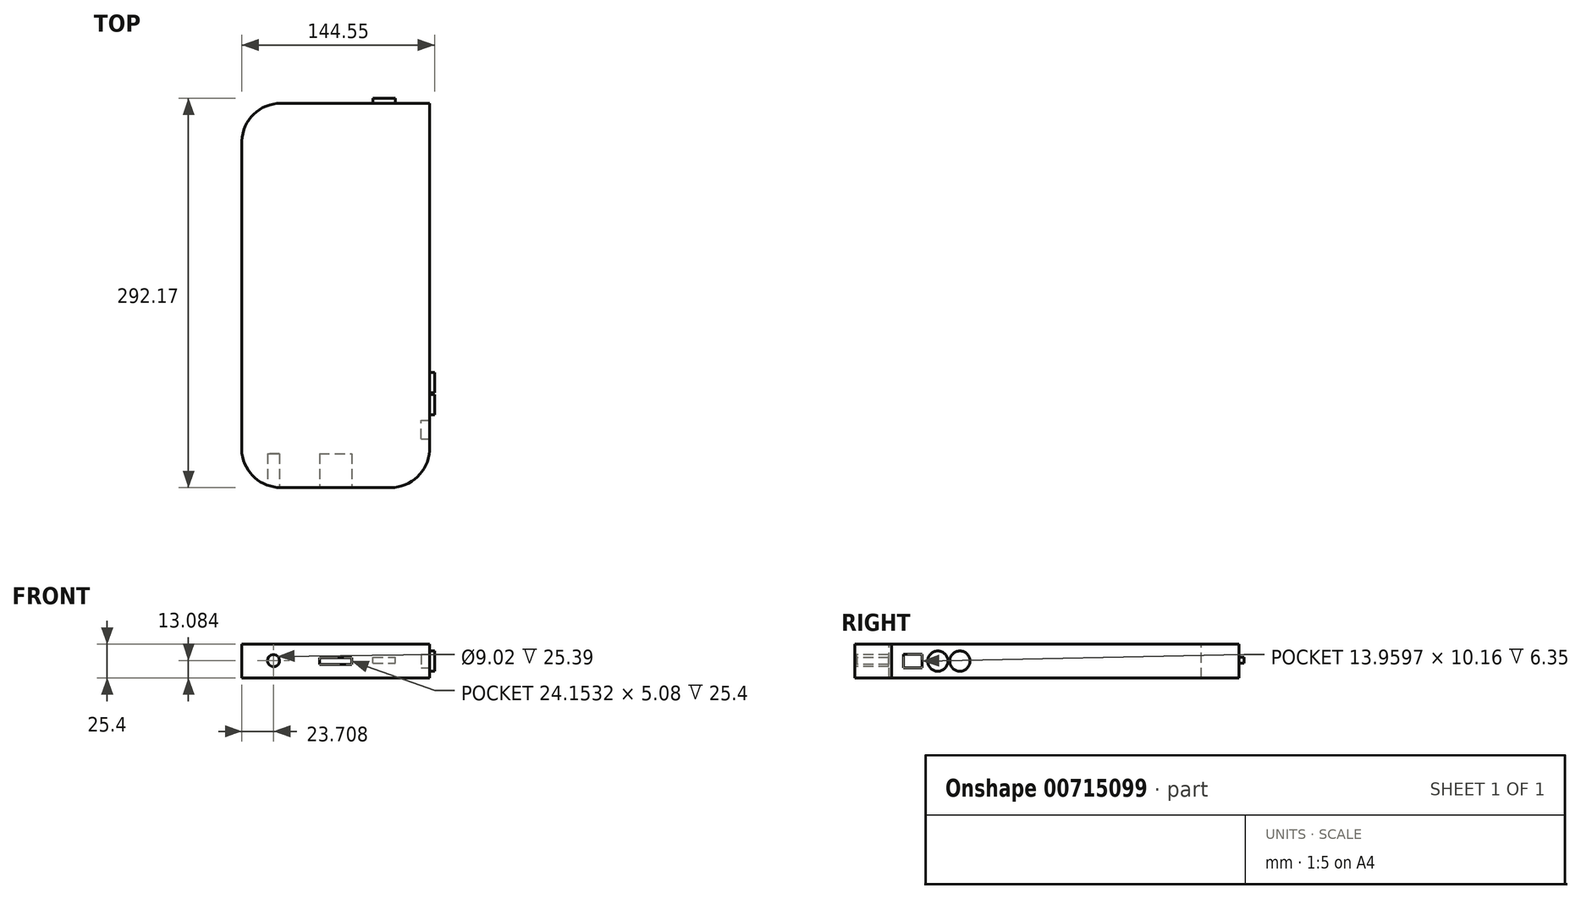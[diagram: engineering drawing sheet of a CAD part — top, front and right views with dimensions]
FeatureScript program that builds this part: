
annotation { "Feature Type Name" : "Feature", "Feature Type Description" : "" }
export const myFeature = defineFeature(function(context is Context, id is Id, definition is map)
    precondition{}
    {
        {
            var Q0;
            Q0=qCreatedBy(makeId("Top.planeOp"),FACE);
            var sketch = newSketch(context, id + "F0", { "sketchPlane" : qUnion([Q0])});
            skLineSegment(sketch, "E0.bottom", {"start": v(-74.1, 116.3) * mm, "end": v(66.65, 116.3) * mm});
            skLineSegment(sketch, "E0.top", {"start": v(-74.1, -172.07) * mm, "end": v(66.65, -172.07) * mm});
            skLineSegment(sketch, "E0.left", {"start": v(-74.1, 116.3) * mm, "end": v(-74.1, -172.07) * mm});
            skLineSegment(sketch, "E0.right", {"start": v(66.65, 116.3) * mm, "end": v(66.65, -172.07) * mm});
            skSolve(sketch);
        }
        {
            var Q0;
            Q0 = qSketchRegion(id + "F0", true);
            extrude(context, id + "F1", {"entities" : qUnion([Q0]), "depth" : 25.4 * mm, "offsetDistance" : 25.4 * mm});
        }
        {
            var Q0;
            Q0=makeQuery(id+"F1.opExtrude","CAP_FACE",FACE,{"disambiguationData":[OSD([sQuery(id+"F0.wireOp",EDGE,"E0.bottom"),sQuery(id+"F0.wireOp",EDGE,"E0.top"),sQuery(id+"F0.wireOp",EDGE,"E0.left"),sQuery(id+"F0.wireOp",EDGE,"E0.right")])],"isStart":false});
            var sketch = newSketch(context, id + "F2", { "sketchPlane" : qUnion([Q0])});
            skArc(sketch, "E1", {"start": v(37.48, -172.07) * mm, "mid": v(57.6, -164.03) * mm, "end": v(66.65, -144.34) * mm});
            skArc(sketch, "E2", {"start": v(-74.1, -139.36) * mm, "mid": v(-66.95, -162.24) * mm, "end": v(-45.1, -172.07) * mm});
            skArc(sketch, "E3", {"start": v(66.65, 85.36) * mm, "mid": v(57.56, 108.56) * mm, "end": v(33.87, 116.3) * mm});
            skArc(sketch, "E4", {"start": v(-44.9, 116.3) * mm, "mid": v(-65.83, 107.45) * mm, "end": v(-74.1, 86.27) * mm});
            skSolve(sketch);
        }
        {
            var Q0;
            {var subQ7=sQuery(id+"F2.wireOp",EDGE,"E1");Q0=makeQuery(id+"F2.imprint","IMPRINT",FACE,{"disambiguationData":[TD([[makeQuery(id+"F2.imprint","IMPRINT",EDGE,{"derivedFrom":subQ7}),1.0]])]});}
            var sketch = newSketch(context, id + "F3", { "sketchPlane" : qUnion([Q0])});
            skLineSegment(sketch, "E5.bottom", {"start": v(-61.4, -116.5) * mm, "end": v(53.95, -116.5) * mm});
            skLineSegment(sketch, "E5.top", {"start": v(-61.4, 71.84) * mm, "end": v(53.95, 71.84) * mm});
            skLineSegment(sketch, "E5.left", {"start": v(-61.4, -116.5) * mm, "end": v(-61.4, 71.84) * mm});
            skLineSegment(sketch, "E5.right", {"start": v(53.95, -116.5) * mm, "end": v(53.95, 71.84) * mm});
            skCircle(sketch, "E6", {"center": v(-9.17, -146.33) * mm, "radius": 13.88 * mm});
            skArc(sketch, "E7", {"start": v(-43.18, -172.58) * mm, "mid": v(-66.38, -163.17) * mm, "end": v(-73.78, -139.25) * mm});
            skArc(sketch, "E8", {"start": v(67.46, -143.84) * mm, "mid": v(57.83, -163.2) * mm, "end": v(37.53, -170.64) * mm});
            skArc(sketch, "E9", {"start": v(34.57, 116.43) * mm, "mid": v(58.51, 108.08) * mm, "end": v(66.9, 84.15) * mm});
            skArc(sketch, "E10", {"start": v(-45.12, 117.02) * mm, "mid": v(-67.2, 107.18) * mm, "end": v(-74.31, 84.07) * mm});
            skSolve(sketch);
        }
        {
            var Q0;
            {var subQ0=sQuery(id+"F2.wireOp",EDGE,"E1");Q0=makeQuery(id+"F2.imprint","IMPRINT",FACE,{"disambiguationData":[TD([[makeQuery(id+"F2.imprint","IMPRINT",EDGE,{"derivedFrom":subQ0}),-1.0]])]});}
            var Q1;
            {var subQ0=sQuery(id+"F2.wireOp",EDGE,"E2");var subQ1=makeQuery(id+"F1.opExtrude","CAP_EDGE",EDGE,{"disambiguationData":[OSD([sQuery(id+"F0.wireOp",EDGE,"E0.top")])],"isStart":false});var subQ2=makeQuery(id+"F2.imprint","INTERSECT",VERTEX,{"derivedFrom":[subQ1,subQ0]});Q1=makeQuery(id+"F2.imprint","IMPRINT",FACE,{"disambiguationData":[TD([[makeQuery(id+"F2.imprint","IMPRINT",EDGE,{"disambiguationData":[TD([[subQ2,1.0]])],"derivedFrom":subQ0}),-1.0]])]});}
            var Q2;
            {var subQ0=sQuery(id+"F2.wireOp",EDGE,"E3");var subQ1=makeQuery(id+"F1.opExtrude","CAP_EDGE",EDGE,{"disambiguationData":[OSD([sQuery(id+"F0.wireOp",EDGE,"E0.right")])],"isStart":false});var subQ2=makeQuery(id+"F2.imprint","INTERSECT",VERTEX,{"disambiguationData":[OD(1.0)],"derivedFrom":[subQ1,subQ0]});Q2=makeQuery(id+"F2.imprint","IMPRINT",FACE,{"disambiguationData":[TD([[makeQuery(id+"F2.imprint","IMPRINT",EDGE,{"disambiguationData":[TD([[subQ2,-1.0]])],"derivedFrom":subQ0}),-1.0]])]});}
            var Q3;
            {var subQ0=sQuery(id+"F2.wireOp",EDGE,"E4");var subQ1=makeQuery(id+"F1.opExtrude","CAP_EDGE",EDGE,{"disambiguationData":[OSD([sQuery(id+"F0.wireOp",EDGE,"E0.bottom")])],"isStart":false});var subQ2=makeQuery(id+"F2.imprint","INTERSECT",VERTEX,{"derivedFrom":[subQ1,subQ0]});Q3=makeQuery(id+"F2.imprint","IMPRINT",FACE,{"disambiguationData":[TD([[makeQuery(id+"F2.imprint","IMPRINT",EDGE,{"disambiguationData":[TD([[subQ2,-1.0]])],"derivedFrom":subQ0}),-1.0]])]});}
            extrude(context, id + "F4", {"entities" : qUnion([Q0, Q1, Q2, Q3]), "operationType" : NewBodyOperationType.REMOVE, "oppositeDirection" : true, "depth" : 25.4 * mm, "offsetDistance" : 25.4 * mm});
        }
        {
            var Q0;
            Q0=makeQuery(id+"F1.opExtrude","SWEPT_FACE",FACE,{"disambiguationData":[OSD([sQuery(id+"F0.wireOp",EDGE,"E0.top")])]});
            var sketch = newSketch(context, id + "F5", { "sketchPlane" : qUnion([Q0])});
            skLineSegment(sketch, "E11.bottom", {"start": v(-15.88, 15.24) * mm, "end": v(8.27, 15.24) * mm});
            skLineSegment(sketch, "E11.top", {"start": v(-15.88, 10.16) * mm, "end": v(8.27, 10.16) * mm});
            skLineSegment(sketch, "E11.left", {"start": v(-15.88, 15.24) * mm, "end": v(-15.88, 10.16) * mm});
            skLineSegment(sketch, "E11.right", {"start": v(8.27, 15.24) * mm, "end": v(8.27, 10.16) * mm});
            skPoint(sketch, "E12", {"position": v(-20.9, 13.08) * mm});
            skPoint(sketch, "E13", {"position": v(13.99, 13.08) * mm});
            skPoint(sketch, "E14", {"position": v(-24.21, 15.24) * mm});
            skPoint(sketch, "E15", {"position": v(-24.21, 10.16) * mm});
            skPoint(sketch, "E16", {"position": v(-28.42, 15.24) * mm});
            skPoint(sketch, "E17", {"position": v(-28.12, 10.16) * mm});
            skPoint(sketch, "E18", {"position": v(-31.73, 15.24) * mm});
            skPoint(sketch, "E19", {"position": v(-32.03, 10.16) * mm});
            skPoint(sketch, "E20", {"position": v(-35.64, 15.24) * mm});
            skPoint(sketch, "E21", {"position": v(-35.64, 10.16) * mm});
            skPoint(sketch, "E22", {"position": v(-39.55, 15.24) * mm});
            skPoint(sketch, "E23", {"position": v(-40.16, 10.16) * mm});
            skPoint(sketch, "E24", {"position": v(17, 15.24) * mm});
            skPoint(sketch, "E25", {"position": v(16.7, 10.16) * mm});
            skPoint(sketch, "E26", {"position": v(21.2, 15.24) * mm});
            skPoint(sketch, "E27", {"position": v(20.6, 10.16) * mm});
            skPoint(sketch, "E28", {"position": v(24.21, 15.24) * mm});
            skPoint(sketch, "E29", {"position": v(24.21, 10.16) * mm});
            skPoint(sketch, "E30", {"position": v(28.12, 15.24) * mm});
            skPoint(sketch, "E31", {"position": v(27.82, 10.16) * mm});
            skCircle(sketch, "E32", {"center": v(-50.38, 13.08) * mm, "radius": 4.51 * mm});
            skSolve(sketch);
        }
        {
            var Q0;
            Q0=makeQuery(id+"F1.opExtrude","SWEPT_FACE",FACE,{"disambiguationData":[OSD([sQuery(id+"F0.wireOp",EDGE,"E0.bottom")])]});
            var sketch = newSketch(context, id + "F6", { "sketchPlane" : qUnion([Q0])});
            skLineSegment(sketch, "E33.bottom", {"start": v(-24.21, 10.98) * mm, "end": v(-41.15, 10.98) * mm});
            skLineSegment(sketch, "E33.top", {"start": v(-24.21, 15.5) * mm, "end": v(-41.15, 15.5) * mm});
            skLineSegment(sketch, "E33.left", {"start": v(-24.21, 10.98) * mm, "end": v(-24.21, 15.5) * mm});
            skLineSegment(sketch, "E33.right", {"start": v(-41.15, 10.98) * mm, "end": v(-41.15, 15.5) * mm});
            skSolve(sketch);
        }
        {
            var Q0;
            Q0=makeQuery(id+"F6.imprint","IMPRINT",FACE,{"disambiguationData":[TD([[makeQuery(id+"F6.imprint","IMPRINT",EDGE,{"derivedFrom":sQuery(id+"F6.wireOp",EDGE,"E33.bottom")}),-1.0]])]});
            extrude(context, id + "F7", {"entities" : qUnion([Q0]), "operationType" : NewBodyOperationType.ADD, "depth" : 3.8 * mm, "offsetDistance" : 25.4 * mm});
        }
        {
            var Q0;
            Q0=makeQuery(id+"F1.opExtrude","SWEPT_FACE",FACE,{"disambiguationData":[OSD([sQuery(id+"F0.wireOp",EDGE,"E0.right")])]});
            var sketch = newSketch(context, id + "F8", { "sketchPlane" : qUnion([Q0])});
            skCircle(sketch, "E34", {"center": v(-109.85, 12.7) * mm, "radius": 7.62 * mm});
            skCircle(sketch, "E35", {"center": v(-93.23, 12.7) * mm, "radius": 7.62 * mm});
            skLineSegment(sketch, "E36.bottom", {"start": v(-135.45, 17.78) * mm, "end": v(-121.49, 17.78) * mm});
            skLineSegment(sketch, "E36.top", {"start": v(-135.45, 7.62) * mm, "end": v(-121.49, 7.62) * mm});
            skLineSegment(sketch, "E36.left", {"start": v(-135.45, 17.78) * mm, "end": v(-135.45, 7.62) * mm});
            skLineSegment(sketch, "E36.right", {"start": v(-121.49, 17.78) * mm, "end": v(-121.49, 7.62) * mm});
            skSolve(sketch);
        }
        {
            var Q0;
            Q0=makeQuery(id+"F8.imprint","IMPRINT",FACE,{"disambiguationData":[TD([[makeQuery(id+"F8.imprint","IMPRINT",EDGE,{"derivedFrom":sQuery(id+"F8.wireOp",EDGE,"E36.bottom")}),-1.0]])]});
            extrude(context, id + "F9", {"entities" : qUnion([Q0]), "operationType" : NewBodyOperationType.REMOVE, "oppositeDirection" : true, "depth" : 6.35 * mm, "offsetDistance" : 25.4 * mm});
        }
        {
            var Q0;
            Q0=makeQuery(id+"F1.opExtrude","SWEPT_FACE",FACE,{"disambiguationData":[OSD([sQuery(id+"F0.wireOp",EDGE,"E0.right")])]});
            var sketch = newSketch(context, id + "F10", { "sketchPlane" : qUnion([Q0])});
            skSolve(sketch);
        }
        {
            var Q0;
            Q0=makeQuery(id+"F8.imprint","IMPRINT",FACE,{"disambiguationData":[TD([[makeQuery(id+"F8.imprint","IMPRINT",EDGE,{"derivedFrom":sQuery(id+"F8.wireOp",EDGE,"E34")}),1.0]])]});
            var Q1;
            Q1=makeQuery(id+"F8.imprint","IMPRINT",FACE,{"disambiguationData":[TD([[makeQuery(id+"F8.imprint","IMPRINT",EDGE,{"derivedFrom":sQuery(id+"F8.wireOp",EDGE,"E35")}),1.0]])]});
            extrude(context, id + "F11", {"entities" : qUnion([Q0, Q1]), "operationType" : NewBodyOperationType.ADD, "depth" : 3.8 * mm, "offsetDistance" : 25.4 * mm});
        }
        {
            var Q0;
            Q0=makeQuery(id+"F5.imprint","IMPRINT",FACE,{"disambiguationData":[TD([[makeQuery(id+"F5.imprint","IMPRINT",EDGE,{"derivedFrom":sQuery(id+"F5.wireOp",EDGE,"E11.bottom")}),-1.0]])]});
            extrude(context, id + "F12", {"entities" : qUnion([Q0]), "operationType" : NewBodyOperationType.REMOVE, "oppositeDirection" : true, "depth" : 25.4 * mm, "offsetDistance" : 25.4 * mm});
        }
        {
            var Q0;
            Q0=makeQuery(id+"F5.imprint","IMPRINT",FACE,{"disambiguationData":[TD([[makeQuery(id+"F5.imprint","IMPRINT",EDGE,{"derivedFrom":sQuery(id+"F5.wireOp",EDGE,"E32")}),1.0]])]});
            extrude(context, id + "F13", {"entities" : qUnion([Q0]), "operationType" : NewBodyOperationType.REMOVE, "oppositeDirection" : true, "depth" : 25.4 * mm, "offsetDistance" : 25.4 * mm});
        }
    });
